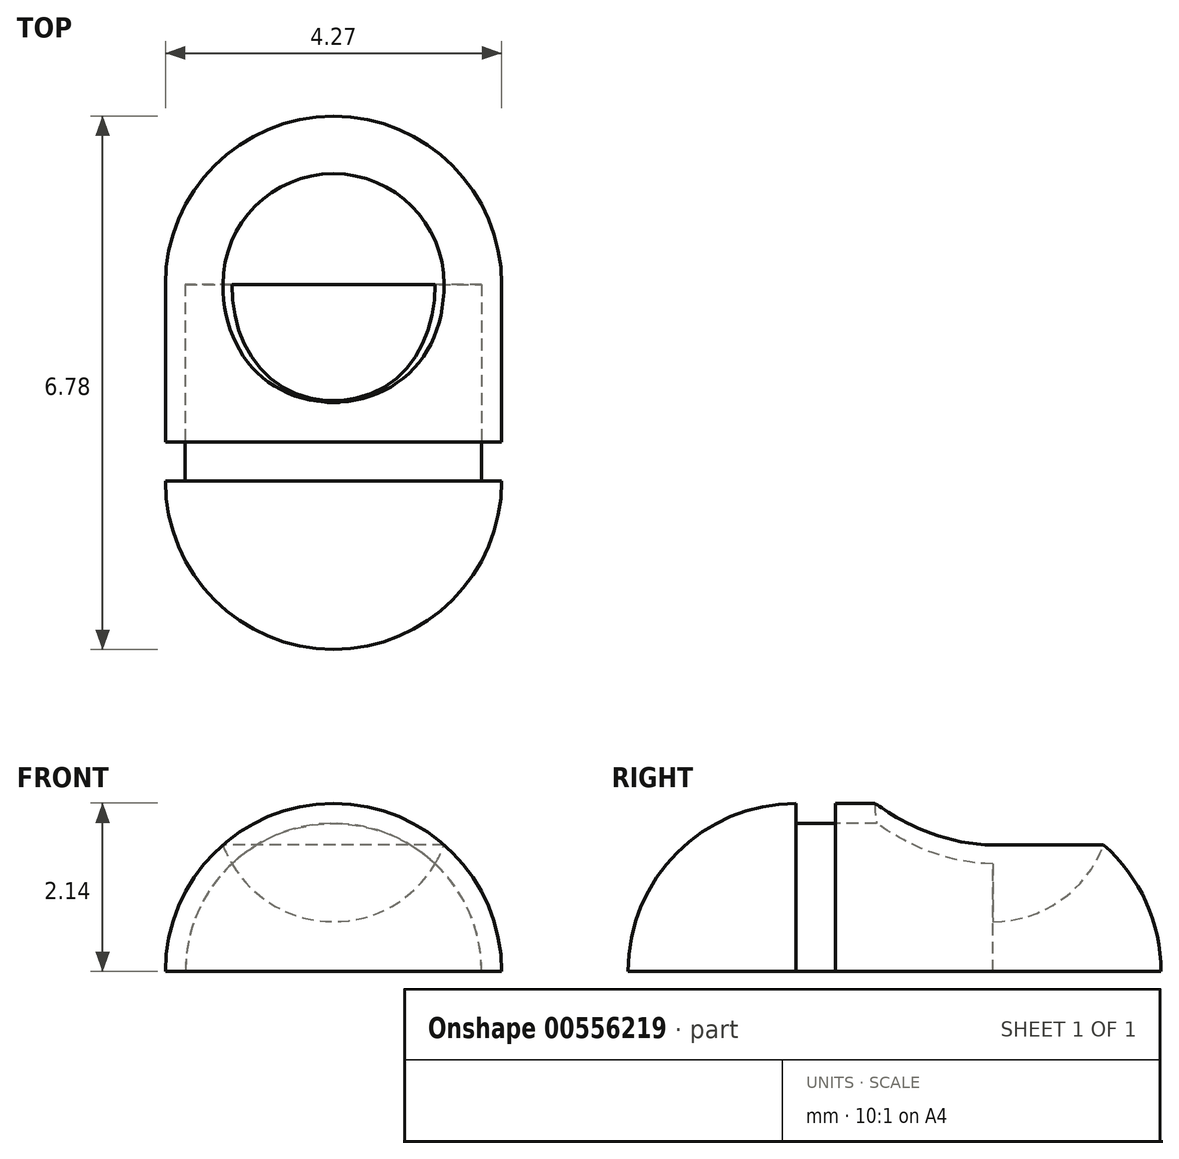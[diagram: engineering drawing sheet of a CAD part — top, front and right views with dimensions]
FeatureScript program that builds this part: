
annotation { "Feature Type Name" : "Feature", "Feature Type Description" : "" }
export const myFeature = defineFeature(function(context is Context, id is Id, definition is map)
    precondition{}
    {
        {
            var Q0;
            Q0=qCreatedBy(makeId("Front.planeOp"),FACE);
            var sketch = newSketch(context, id + "F0", { "sketchPlane" : qUnion([Q0])});
            skLineSegment(sketch, "E0", {"start": v(0, 0) * mm, "end": v(12.5, 0) * mm, "construction": true});
            skLineSegment(sketch, "E1", {"start": v(12.5, 0) * mm, "end": v(0, 0) * mm, "construction": true});
            skLineSegment(sketch, "E2", {"start": v(-12.88, 0) * mm, "end": v(0, 0) * mm, "construction": true});
            skArc(sketch, "E3", {"start": v(-6.44, 0) * mm, "mid": v(-8.58, 2.14) * mm, "end": v(-10.71, 0) * mm});
            skPoint(sketch, "E3.startSnap0", {"position": v(-6.44, 0) * mm});
            skArc(sketch, "E4", {"start": v(-6.7, 0) * mm, "mid": v(-8.58, 1.88) * mm, "end": v(-10.46, 0) * mm});
            skLineSegment(sketch, "E5", {"start": v(-6.44, 0) * mm, "end": v(-10.71, 0) * mm});
            skLineSegment(sketch, "E6", {"start": v(-8.58, 0) * mm, "end": v(-8.58, 2.14) * mm, "construction": true});
            skSolve(sketch);
        }
        {
            var Q0;
            Q0=qCreatedBy(makeId("Top.planeOp"),FACE);
            var sketch = newSketch(context, id + "F1", { "sketchPlane" : qUnion([Q0])});
            skArc(sketch, "E7", {"start": v(-10.71, 0) * mm, "mid": v(-8.58, -2.14) * mm, "end": v(-6.44, 0) * mm});
            skLineSegment(sketch, "E8", {"start": v(-10.71, 0) * mm, "end": v(-6.44, 0) * mm});
            skSolve(sketch);
        }
        {
            var Q0;
            Q0=makeQuery(id+"F1.imprint","IMPRINT",FACE,{"disambiguationData":[TD([[makeQuery(id+"F1.imprint","IMPRINT",EDGE,{"derivedFrom":sQuery(id+"F1.wireOp",EDGE,"E7")}),1.0]])]});
            var Q1;
            Q1=sQuery(id+"F1.wireOp",EDGE,"E8");
            revolve(context, id + "F2", {"entities" : qUnion([Q0]), "axis" : qUnion([Q1]), "revolveType" : RevolveType.ONE_DIRECTION, "oppositeDirection" : true, "angle" : 90 * degree});
        }
        {
            var Q0;
            {var subQ0=sQuery(id+"F0.wireOp",EDGE,"E4");Q0=makeQuery(id+"F0.imprint","IMPRINT",FACE,{"disambiguationData":[TD([[makeQuery(id+"F0.imprint","IMPRINT",EDGE,{"derivedFrom":subQ0}),1.0]])]});}
            extrude(context, id + "F3", {"entities" : qUnion([Q0]), "operationType" : NewBodyOperationType.ADD, "oppositeDirection" : true, "depth" : .5 * mm, "offsetDistance" : 25.4 * mm});
        }
        {
            var Q0;
            Q0=makeQuery(id+"F3.opExtrude","CAP_FACE",FACE,{"disambiguationData":[OSD([sQuery(id+"F0.wireOp",EDGE,"E4"),sQuery(id+"F0.wireOp",EDGE,"E5")])],"isStart":false});
            var sketch = newSketch(context, id + "F4", { "sketchPlane" : qUnion([Q0])});
            skArc(sketch, "E9", {"start": v(10.71, 0) * mm, "mid": v(8.58, 2.14) * mm, "end": v(6.44, 0) * mm});
            skLineSegment(sketch, "E10", {"start": v(6.44, 0) * mm, "end": v(10.71, 0) * mm});
            skSolve(sketch);
        }
        {
            var Q0;
            {var subQ0=sQuery(id+"F4.wireOp",EDGE,"E9");Q0=makeQuery(id+"F4.imprint","IMPRINT",FACE,{"disambiguationData":[TD([[makeQuery(id+"F4.imprint","IMPRINT",EDGE,{"derivedFrom":subQ0}),1.0]])]});}
            extrude(context, id + "F5", {"entities" : qUnion([Q0]), "depth" : 2 * mm, "offsetDistance" : 25.4 * mm});
        }
        {
            var Q0;
            Q0=qCreatedBy(makeId("Top.planeOp"),FACE);
            var sketch = newSketch(context, id + "F6", { "sketchPlane" : qUnion([Q0])});
            skArc(sketch, "E11", {"start": v(-6.44, 2.5) * mm, "mid": v(-8.58, 4.64) * mm, "end": v(-10.71, 2.5) * mm});
            skLineSegment(sketch, "E12", {"start": v(-10.71, 2.5) * mm, "end": v(-6.44, 2.5) * mm});
            skSolve(sketch);
        }
        {
            var Q0;
            Q0=makeQuery(id+"F6.imprint","IMPRINT",FACE,{"disambiguationData":[TD([[makeQuery(id+"F6.imprint","IMPRINT",EDGE,{"derivedFrom":sQuery(id+"F6.wireOp",EDGE,"E11")}),1.0]])]});
            var Q1;
            Q1=sQuery(id+"F6.wireOp",EDGE,"E12");
            revolve(context, id + "F7", {"operationType" : NewBodyOperationType.ADD, "entities" : qUnion([Q0]), "axis" : qUnion([Q1]), "revolveType" : RevolveType.ONE_DIRECTION, "angle" : 90 * degree});
        }
        {
            var Q0;
            Q0=qCreatedBy(makeId("Top.planeOp"),FACE);
            cPlane(context, id + "F8", {"entities" : qUnion([Q0]), "cplaneType" : CPlaneType.OFFSET, "offset" : 2.13 * mm, "width" : 152.4 * mm, "height" : 152.4 * mm});
        }
        {
            var Q0;
            Q0=qCreatedBy(id+"F8.planeOp",FACE);
            var sketch = newSketch(context, id + "F9", { "sketchPlane" : qUnion([Q0])});
            skLineSegment(sketch, "E13.0", {"start": v(-10.71, 2.5) * mm, "end": v(-6.44, 2.5) * mm});
            skPoint(sketch, "E14.0", {"position": v(-8.58, 0.5) * mm});
            skPoint(sketch, "E15.0", {"position": v(-8.58, 4.64) * mm});
            skLineSegment(sketch, "E16", {"start": v(-8.58, 0.5) * mm, "end": v(-8.58, 4.64) * mm, "construction": true});
            skArc(sketch, "E17", {"start": v(-7.08, 2.5) * mm, "mid": v(-8.58, 4) * mm, "end": v(-10.08, 2.5) * mm});
            skLineSegment(sketch, "E18", {"start": v(-10.71, 2.5) * mm, "end": v(-6.44, 2.5) * mm, "construction": true});
            skSolve(sketch);
        }
        {
            var Q0;
            {var subQ0=sQuery(id+"F9.wireOp",EDGE,"E17");Q0=makeQuery(id+"F9.imprint","IMPRINT",FACE,{"disambiguationData":[TD([[makeQuery(id+"F9.imprint","IMPRINT",EDGE,{"derivedFrom":subQ0}),1.0]])]});}
            var Q1;
            Q1=sQuery(id+"F9.wireOp",EDGE,"E13.0");
            revolve(context, id + "F10", {"operationType" : NewBodyOperationType.REMOVE, "entities" : qUnion([Q0]), "axis" : qUnion([Q1]), "revolveType" : RevolveType.FULL, "oppositeDirection" : true});
        }
    });
